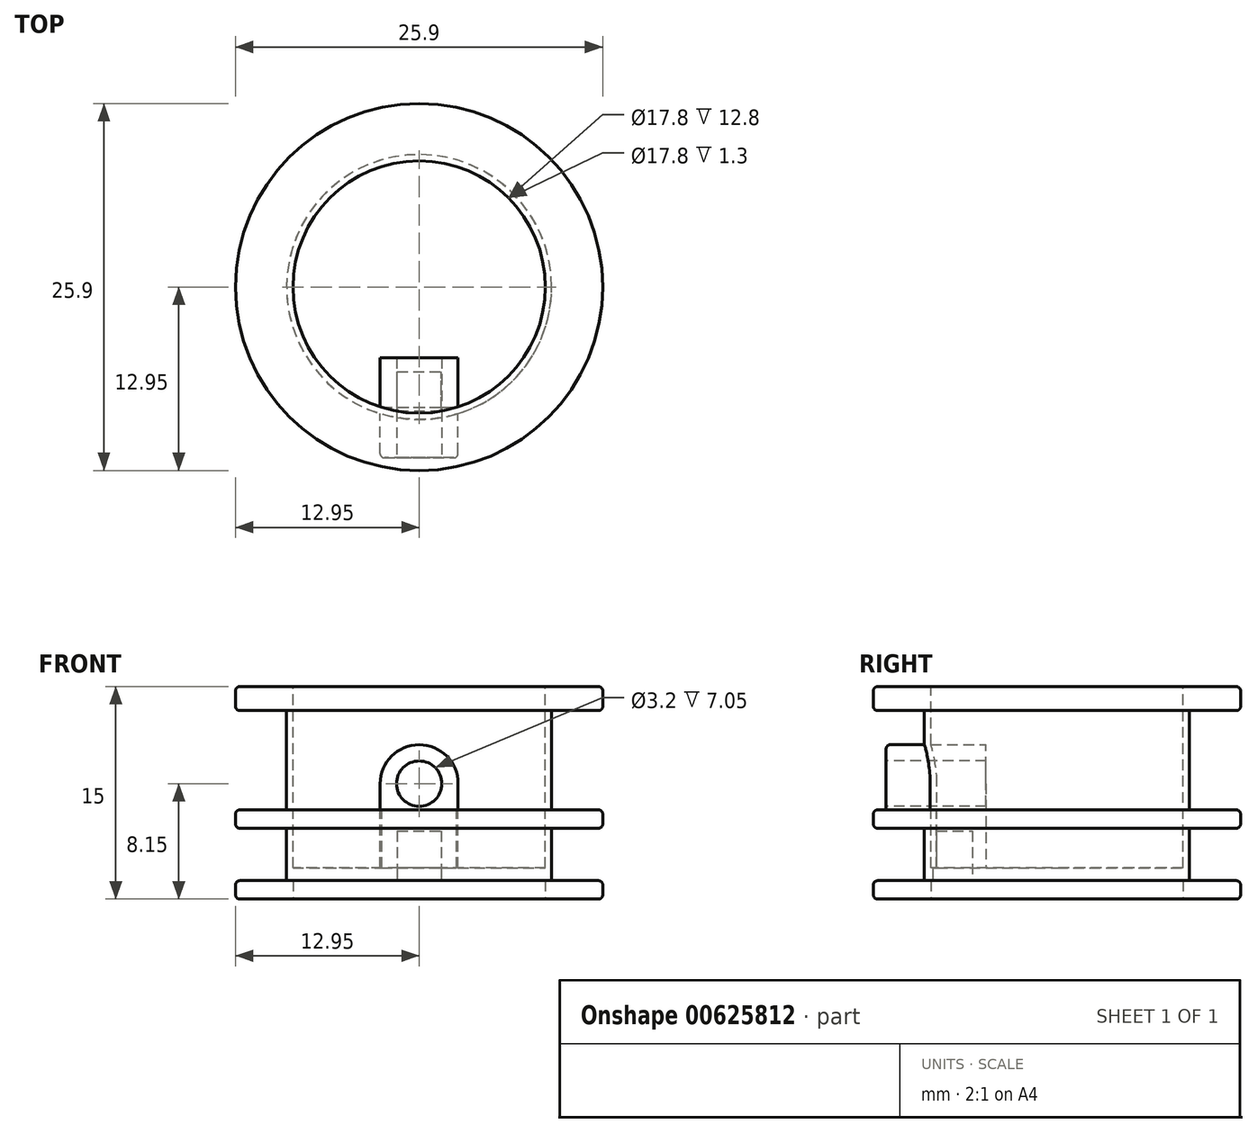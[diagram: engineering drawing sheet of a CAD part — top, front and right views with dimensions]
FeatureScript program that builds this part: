
annotation { "Feature Type Name" : "Feature", "Feature Type Description" : "" }
export const myFeature = defineFeature(function(context is Context, id is Id, definition is map)
    precondition{}
    {
        {
            var Q0;
            Q0=qCreatedBy(makeId("Front.planeOp"),FACE);
            var sketch = newSketch(context, id + "F0", { "sketchPlane" : qUnion([Q0])});
            skLineSegment(sketch, "E0", {"start": v(0, 0) * mm, "end": v(-12.95, 0) * mm});
            skLineSegment(sketch, "E1", {"start": v(-12.95, 0) * mm, "end": v(-12.95, 1.3) * mm});
            skLineSegment(sketch, "E2", {"start": v(-12.95, 1.3) * mm, "end": v(-9.35, 1.3) * mm});
            skLineSegment(sketch, "E3", {"start": v(-9.35, 1.3) * mm, "end": v(-9.35, 5) * mm});
            skLineSegment(sketch, "E4", {"start": v(-9.35, 5) * mm, "end": v(-12.95, 5) * mm});
            skLineSegment(sketch, "E5", {"start": v(-12.95, 5) * mm, "end": v(-12.95, 6.3) * mm});
            skLineSegment(sketch, "E6", {"start": v(-12.95, 6.3) * mm, "end": v(-9.35, 6.3) * mm});
            skLineSegment(sketch, "E7", {"start": v(-9.35, 6.3) * mm, "end": v(-9.35, 13.3) * mm});
            skLineSegment(sketch, "E8", {"start": v(-9.35, 13.3) * mm, "end": v(-12.95, 13.3) * mm});
            skLineSegment(sketch, "E9", {"start": v(-12.95, 13.3) * mm, "end": v(-12.95, 15) * mm});
            skLineSegment(sketch, "E10", {"start": v(-12.95, 15) * mm, "end": v(0, 15) * mm});
            skLineSegment(sketch, "E11", {"start": v(0, 15) * mm, "end": v(0, 0) * mm});
            skSolve(sketch);
        }
        {
            var Q0;
            Q0=makeQuery(id+"F0.imprint","IMPRINT",FACE,{"disambiguationData":[TD([[makeQuery(id+"F0.imprint","IMPRINT",EDGE,{"derivedFrom":sQuery(id+"F0.wireOp",EDGE,"E0")}),-1.0]])]});
            var Q1;
            Q1=sQuery(id+"F0.wireOp",EDGE,"E11");
            revolve(context, id + "F1", {"entities" : qUnion([Q0]), "axis" : qUnion([Q1]), "revolveType" : RevolveType.FULL});
        }
        {
            var Q0;
            Q0=makeQuery(id+"F1.opRevolve","SWEPT_FACE",FACE,{"disambiguationData":[OSD([sQuery(id+"F0.wireOp",EDGE,"E0")])]});
            var sketch = newSketch(context, id + "F2", { "sketchPlane" : qUnion([Q0])});
            skCircle(sketch, "E12", {"center": v(0, 0) * mm, "radius": 8.9 * mm});
            skSolve(sketch);
        }
        {
            var Q0;
            Q0 = qSketchRegion(id + "F2", true);
            extrude(context, id + "F3", {"entities" : qUnion([Q0]), "operationType" : NewBodyOperationType.REMOVE, "oppositeDirection" : true, "depth" : 1.3 * mm, "offsetDistance" : 25 * mm});
        }
        {
            var Q0;
            Q0=makeQuery(id+"F1.opRevolve","SWEPT_FACE",FACE,{"disambiguationData":[OSD([sQuery(id+"F0.wireOp",EDGE,"E10")])]});
            var sketch = newSketch(context, id + "F4", { "sketchPlane" : qUnion([Q0])});
            skCircle(sketch, "E13", {"center": v(0, 0) * mm, "radius": 8.9 * mm});
            skSolve(sketch);
        }
        {
            var Q0;
            Q0=makeQuery(id+"F4.imprint","IMPRINT",FACE,{"disambiguationData":[TD([[makeQuery(id+"F4.imprint","IMPRINT",EDGE,{"derivedFrom":sQuery(id+"F4.wireOp",EDGE,"E13")}),1.0]])]});
            extrude(context, id + "F5", {"entities" : qUnion([Q0]), "operationType" : NewBodyOperationType.REMOVE, "oppositeDirection" : true, "depth" : 12.8 * mm, "offsetDistance" : 25 * mm});
        }
        {
            var Q0;
            Q0=qCreatedBy(makeId("Front.planeOp"),FACE);
            var sketch = newSketch(context, id + "F6", { "sketchPlane" : qUnion([Q0])});
            skArc(sketch, "E14", {"start": v(2.75, 8.15) * mm, "mid": v(0, 10.9) * mm, "end": v(-2.75, 8.15) * mm});
            skLineSegment(sketch, "E15", {"start": v(2.75, 8.15) * mm, "end": v(2.75, 6.3) * mm});
            skLineSegment(sketch, "E16", {"start": v(-2.75, 8.15) * mm, "end": v(-2.75, 6.3) * mm});
            skLineSegment(sketch, "E17.0", {"start": v(-12.95, 6.3) * mm, "end": v(12.95, 6.3) * mm});
            skPoint(sketch, "E18", {"position": v(-2.75, 6.3) * mm});
            skPoint(sketch, "E19", {"position": v(2.75, 6.3) * mm});
            skLineSegment(sketch, "E20", {"start": v(-2.75, 6.3) * mm, "end": v(2.75, 6.3) * mm});
            skLineSegment(sketch, "E21.0", {"start": v(-12.95, 1.3) * mm, "end": v(-2.75, 1.3) * mm});
            skLineSegment(sketch, "E22", {"start": v(2.75, 1.3) * mm, "end": v(-2.75, 1.3) * mm});
            skLineSegment(sketch, "E23.trimOffspring", {"start": v(2.75, 1.3) * mm, "end": v(12.95, 1.3) * mm});
            skSolve(sketch);
        }
        {
            var Q0;
            Q0 = qSketchRegion(id + "F6", true);
            extrude(context, id + "F7", {"entities" : qUnion([Q0]), "operationType" : NewBodyOperationType.ADD, "depth" : 12.05 * mm, "offsetDistance" : 25 * mm, "hasSecondDirection" : true, "secondDirectionOppositeDirection" : false, "secondDirectionDepth" : 5 * mm});
        }
        {
            var Q0;
            Q0=qCreatedBy(makeId("Front.planeOp"),FACE);
            var sketch = newSketch(context, id + "F8", { "sketchPlane" : qUnion([Q0])});
            skLineSegment(sketch, "E24.0.0", {"start": v(-2.75, 8.15) * mm, "end": v(-2.75, 6.3) * mm});
            skLineSegment(sketch, "E24.0.1", {"start": v(-2.75, 6.3) * mm, "end": v(2.75, 6.3) * mm});
            skLineSegment(sketch, "E24.0.2", {"start": v(2.75, 6.3) * mm, "end": v(2.75, 8.15) * mm});
            skArc(sketch, "E24.0.3", {"start": v(2.75, 8.15) * mm, "mid": v(0, 10.9) * mm, "end": v(-2.75, 8.15) * mm});
            skLineSegment(sketch, "E25", {"start": v(12.95, 6.3) * mm, "end": v(12.95, 5) * mm});
            skLineSegment(sketch, "E26", {"start": v(-12.95, 5) * mm, "end": v(-12.95, 6.3) * mm});
            skLineSegment(sketch, "E27.0", {"start": v(-12.95, 5) * mm, "end": v(12.95, 5) * mm});
            skLineSegment(sketch, "E28.0", {"start": v(-12.95, 1.3) * mm, "end": v(12.95, 1.3) * mm});
            skLineSegment(sketch, "E29", {"start": v(-2.75, 6.3) * mm, "end": v(-2.75, 1.3) * mm});
            skLineSegment(sketch, "E30", {"start": v(2.75, 6.3) * mm, "end": v(2.75, 1.3) * mm});
            skLineSegment(sketch, "E31", {"start": v(2.75, 1.3) * mm, "end": v(-2.75, 1.3) * mm});
            skSolve(sketch);
        }
        {
            var Q0;
            Q0 = qSketchRegion(id + "F8", true);
            extrude(context, id + "F9", {"entities" : qUnion([Q0]), "operationType" : NewBodyOperationType.ADD, "depth" : 8.5 * mm, "offsetDistance" : 25 * mm, "hasSecondDirection" : true, "secondDirectionOppositeDirection" : false, "secondDirectionDepth" : 5 * mm});
        }
        {
            var Q0;
            Q0=makeQuery(id+"F7.opExtrude","CAP_FACE",FACE,{"disambiguationData":[OSD([sQuery(id+"F6.wireOp",EDGE,"E14"),sQuery(id+"F6.wireOp",EDGE,"E15"),sQuery(id+"F6.wireOp",EDGE,"E16"),sQuery(id+"F6.wireOp",EDGE,"E20")])],"isStart":false});
            var sketch = newSketch(context, id + "F10", { "sketchPlane" : qUnion([Q0])});
            skArc(sketch, "E32.0", {"start": v(2.75, 8.15) * mm, "mid": v(0, 10.9) * mm, "end": v(-2.75, 8.15) * mm});
            skCircle(sketch, "E33", {"center": v(0, 8.15) * mm, "radius": 1.6 * mm});
            skSolve(sketch);
        }
        {
            var Q0;
            Q0 = qSketchRegion(id + "F10", true);
            var Q1;
            Q1=makeQuery(id+"F9.boolean.opBoolean","MERGE",FACE,{"derivedFrom":[makeQuery(id+"F7.opExtrude","CAP_FACE",FACE,{"disambiguationData":[OSD([sQuery(id+"F6.wireOp",EDGE,"E14"),sQuery(id+"F6.wireOp",EDGE,"E15"),sQuery(id+"F6.wireOp",EDGE,"E16"),sQuery(id+"F6.wireOp",EDGE,"E20")])],"isStart":true}),makeQuery(id+"F9.opExtrude","CAP_FACE",FACE,{"disambiguationData":[OSD([sQuery(id+"F8.wireOp",EDGE,"E24.0.0"),sQuery(id+"F8.wireOp",EDGE,"E24.0.2"),sQuery(id+"F8.wireOp",EDGE,"E24.0.3"),sQuery(id+"F8.wireOp",EDGE,"E29"),sQuery(id+"F8.wireOp",EDGE,"E30"),sQuery(id+"F8.wireOp",EDGE,"E31")])],"isStart":true})]});
            extrude(context, id + "F11", {"entities" : qUnion([Q0]), "operationType" : NewBodyOperationType.REMOVE, "endBound" : BoundingType.UP_TO_SURFACE, "oppositeDirection" : true, "depth" : 25 * mm, "endBoundEntityFace" : qUnion([Q1]), "offsetDistance" : 25 * mm});
        }
        {
            var Q0;
            Q0=makeQuery(id+"F3.boolean.opBoolean","COPY",FACE,{"derivedFrom":makeQuery(id+"F3.opExtrude","CAP_FACE",FACE,{"disambiguationData":[OSD([sQuery(id+"F2.wireOp",EDGE,"E12")])],"isStart":false})});
            var sketch = newSketch(context, id + "F12", { "sketchPlane" : qUnion([Q0])});
            skLineSegment(sketch, "E34.0", {"start": v(-2.75, 5) * mm, "end": v(2.75, 5) * mm});
            skLineSegment(sketch, "E35.0", {"start": v(-2.75, 8.46) * mm, "end": v(-2.75, 5) * mm});
            skLineSegment(sketch, "E36.0", {"start": v(2.75, 5) * mm, "end": v(2.75, 8.46) * mm});
            skCircle(sketch, "E37.0", {"center": v(0, 0) * mm, "radius": 8.9 * mm});
            skLineSegment(sketch, "E38.bottom", {"start": v(-1.55, 8.76) * mm, "end": v(1.55, 8.76) * mm});
            skLineSegment(sketch, "E38.top", {"start": v(-1.55, 5.96) * mm, "end": v(1.55, 5.96) * mm});
            skLineSegment(sketch, "E38.left", {"start": v(-1.55, 8.76) * mm, "end": v(-1.55, 5.96) * mm});
            skLineSegment(sketch, "E38.right", {"start": v(1.55, 8.76) * mm, "end": v(1.55, 5.96) * mm});
            skSolve(sketch);
        }
        {
            var Q0;
            Q0=makeQuery(id+"F12.imprint","IMPRINT",FACE,{"disambiguationData":[TD([[makeQuery(id+"F12.imprint","IMPRINT",EDGE,{"derivedFrom":sQuery(id+"F12.wireOp",EDGE,"E38.bottom")}),-1.0]])]});
            extrude(context, id + "F13", {"entities" : qUnion([Q0]), "operationType" : NewBodyOperationType.REMOVE, "oppositeDirection" : true, "depth" : 3.5 * mm, "offsetDistance" : 25 * mm});
        }
        {
            var Q0;
            Q0=makeQuery(id+"F1.opRevolve","SWEPT_EDGE",EDGE,{"disambiguationData":[OSD([sQuery(id+"F0.wireOp",EDGE,"E9"),sQuery(id+"F0.wireOp",EDGE,"E10")])]});
            var Q1;
            Q1=makeQuery(id+"F5.boolean.opBoolean","COPY",EDGE,{"derivedFrom":makeQuery(id+"F5.opExtrude","CAP_EDGE",EDGE,{"disambiguationData":[OSD([sQuery(id+"F4.wireOp",EDGE,"E13")])],"isStart":true})});
            var Q2;
            Q2=makeQuery(id+"F1.opRevolve","SWEPT_EDGE",EDGE,{"disambiguationData":[OSD([sQuery(id+"F0.wireOp",EDGE,"E8"),sQuery(id+"F0.wireOp",EDGE,"E9")])]});
            var Q3;
            Q3=makeQuery(id+"F1.opRevolve","SWEPT_EDGE",EDGE,{"disambiguationData":[OSD([sQuery(id+"F0.wireOp",EDGE,"E5"),sQuery(id+"F0.wireOp",EDGE,"E6")])]});
            var Q4;
            Q4=makeQuery(id+"F1.opRevolve","SWEPT_EDGE",EDGE,{"disambiguationData":[OSD([sQuery(id+"F0.wireOp",EDGE,"E4"),sQuery(id+"F0.wireOp",EDGE,"E5")])]});
            var Q5;
            Q5=makeQuery(id+"F1.opRevolve","SWEPT_EDGE",EDGE,{"disambiguationData":[OSD([sQuery(id+"F0.wireOp",EDGE,"E1"),sQuery(id+"F0.wireOp",EDGE,"E2")])]});
            var Q6;
            Q6=makeQuery(id+"F1.opRevolve","SWEPT_EDGE",EDGE,{"disambiguationData":[OSD([sQuery(id+"F0.wireOp",EDGE,"E0"),sQuery(id+"F0.wireOp",EDGE,"E1")])]});
            var Q7;
            Q7=makeQuery(id+"F3.boolean.opBoolean","COPY",EDGE,{"derivedFrom":makeQuery(id+"F3.opExtrude","CAP_EDGE",EDGE,{"disambiguationData":[OSD([sQuery(id+"F2.wireOp",EDGE,"E12")])],"isStart":true})});
            var Q8;
            Q8=makeQuery(id+"FLzKh6KQH3O6TJs_1.1.F7.opExtrude","CAP_EDGE",EDGE,{"disambiguationData":[OSD([sQuery(id+"F6.wireOp",EDGE,"E14")])],"isStart":false});
            var Q9;
            Q9=makeQuery(id+"F7.opExtrude","CAP_EDGE",EDGE,{"disambiguationData":[OSD([sQuery(id+"F6.wireOp",EDGE,"E16")])],"isStart":false});
            fillet(context, id + "F14", {"entities" : qUnion([Q0, Q1, Q2, Q3, Q4, Q5, Q6, Q7, Q8, Q9]), "radius" : 0.3 * mm, "tangentPropagation" : true, "allowEdgeOverflow" : false});
        }
    });
